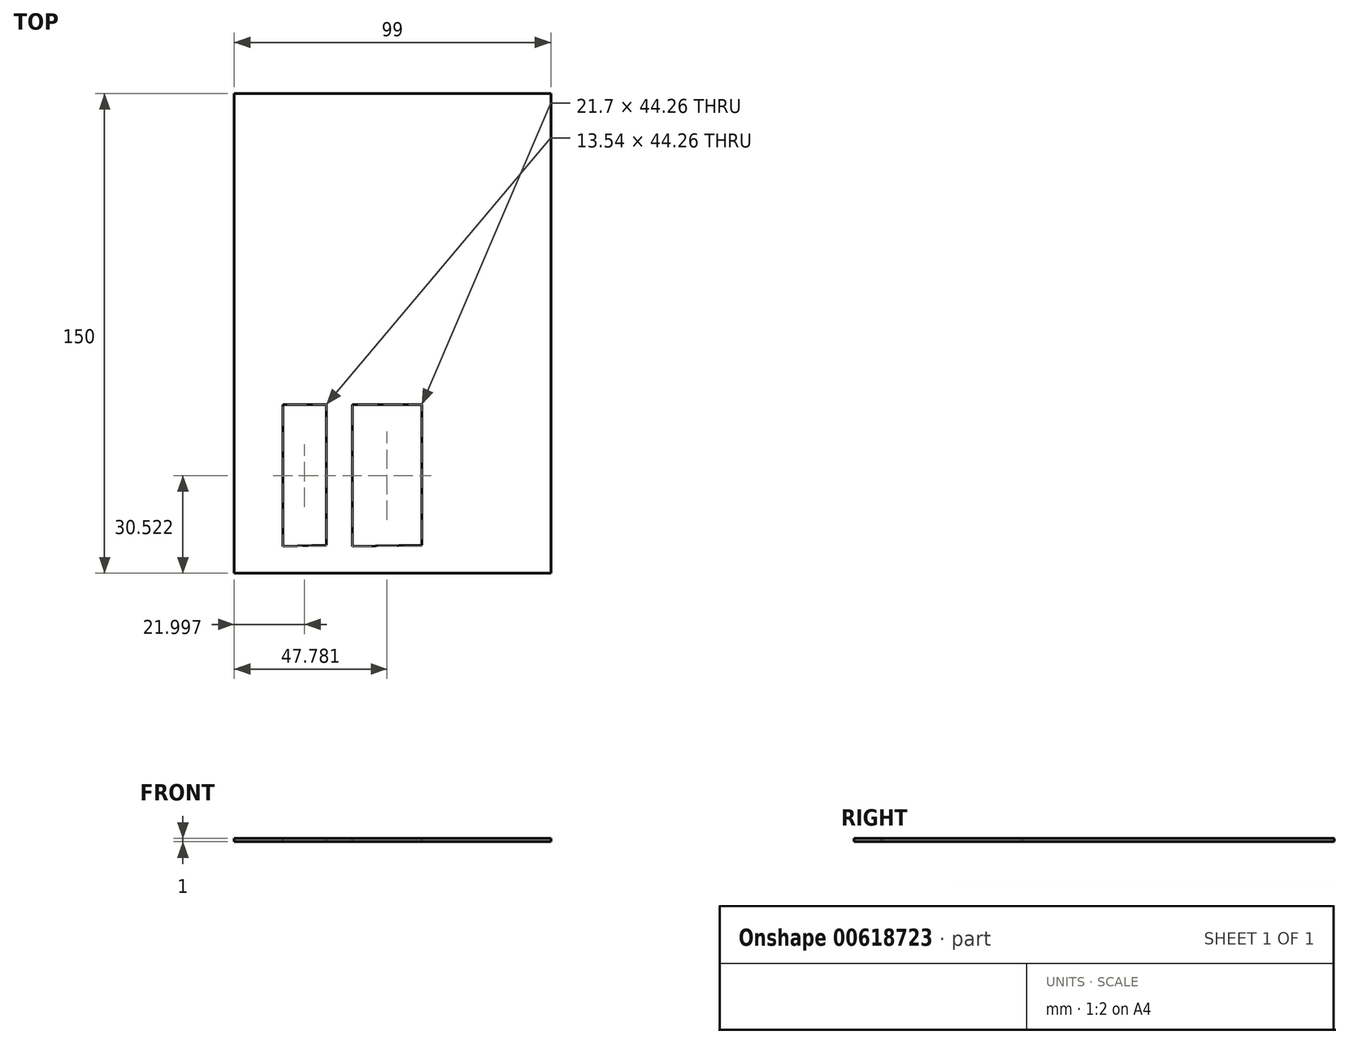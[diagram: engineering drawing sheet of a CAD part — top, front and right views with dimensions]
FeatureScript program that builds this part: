
annotation { "Feature Type Name" : "Feature", "Feature Type Description" : "" }
export const myFeature = defineFeature(function(context is Context, id is Id, definition is map)
    precondition{}
    {
        {
            var Q0;
            Q0=qCreatedBy(makeId("Top.planeOp"),FACE);
            var sketch = newSketch(context, id + "F0", { "sketchPlane" : qUnion([Q0])});
            skLineSegment(sketch, "E0.bottom", {"start": v(-49.5, 75) * mm, "end": v(49.5, 75) * mm});
            skLineSegment(sketch, "E0.top", {"start": v(-49.5, -75) * mm, "end": v(49.5, -75) * mm});
            skLineSegment(sketch, "E0.left", {"start": v(-49.5, 75) * mm, "end": v(-49.5, -75) * mm});
            skLineSegment(sketch, "E0.right", {"start": v(49.5, 75) * mm, "end": v(49.5, -75) * mm});
            skPoint(sketch, "E0.middle", {"position": v(0, 0) * mm});
            skSolve(sketch);
        }
        {
            var Q0;
            Q0 = qSketchRegion(id + "F0", true);
            extrude(context, id + "F1", {"entities" : qUnion([Q0]), "depth" : 1 * mm, "offsetDistance" : 25.4 * mm});
        }
        {
            var Q0;
            Q0=makeQuery(id+"F1.opExtrude","CAP_FACE",FACE,{"disambiguationData":[OSD([sQuery(id+"F0.wireOp",EDGE,"E0.bottom"),sQuery(id+"F0.wireOp",EDGE,"E0.top"),sQuery(id+"F0.wireOp",EDGE,"E0.left"),sQuery(id+"F0.wireOp",EDGE,"E0.right")])],"isStart":false});
            var sketch = newSketch(context, id + "F2", { "sketchPlane" : qUnion([Q0])});
            skLineSegment(sketch, "E1", {"start": v(-34.27, -66.6) * mm, "end": v(-34.27, -22.35) * mm});
            skLineSegment(sketch, "E2", {"start": v(-34.27, -22.35) * mm, "end": v(-20.73, -22.35) * mm});
            skLineSegment(sketch, "E3", {"start": v(-20.73, -22.35) * mm, "end": v(-20.73, -66.18) * mm});
            skLineSegment(sketch, "E4", {"start": v(-34.27, -66.6) * mm, "end": v(-20.73, -66.18) * mm});
            skLineSegment(sketch, "E5", {"start": v(-12.57, -66.6) * mm, "end": v(-12.57, -22.35) * mm});
            skLineSegment(sketch, "E6", {"start": v(-12.57, -22.35) * mm, "end": v(9.13, -22.35) * mm});
            skLineSegment(sketch, "E7", {"start": v(9.13, -22.35) * mm, "end": v(9.13, -66.18) * mm});
            skLineSegment(sketch, "E8", {"start": v(-12.57, -66.6) * mm, "end": v(9.13, -66.18) * mm});
            skLineSegment(sketch, "E9", {"start": v(19.88, -66.18) * mm, "end": v(21.38, -22.35) * mm});
            skLineSegment(sketch, "E10", {"start": v(21.38, -22.35) * mm, "end": v(33.85, -22.77) * mm});
            skLineSegment(sketch, "E11", {"start": v(33.85, -22.77) * mm, "end": v(33.85, -66.6) * mm});
            skLineSegment(sketch, "E12", {"start": v(19.88, -66.18) * mm, "end": v(36.02, -66.73) * mm});
            skLineSegment(sketch, "E13", {"start": v(19.88, -66.18) * mm, "end": v(19.88, -22.77) * mm});
            skLineSegment(sketch, "E14", {"start": v(19.88, -22.77) * mm, "end": v(33.85, -22.77) * mm});
            skSolve(sketch);
        }
        {
            var Q0;
            Q0=makeQuery(id+"F2.imprint","IMPRINT",FACE,{"disambiguationData":[TD([[makeQuery(id+"F2.imprint","IMPRINT",EDGE,{"derivedFrom":sQuery(id+"F2.wireOp",EDGE,"E1")}),-1.0]])]});
            var Q1;
            Q1=makeQuery(id+"F2.imprint","IMPRINT",FACE,{"disambiguationData":[TD([[makeQuery(id+"F2.imprint","IMPRINT",EDGE,{"derivedFrom":sQuery(id+"F2.wireOp",EDGE,"E5")}),-1.0]])]});
            extrude(context, id + "F3", {"entities" : qUnion([Q0, Q1]), "operationType" : NewBodyOperationType.REMOVE, "oppositeDirection" : true, "depth" : 25 * mm, "offsetDistance" : 25 * mm});
        }
    });
